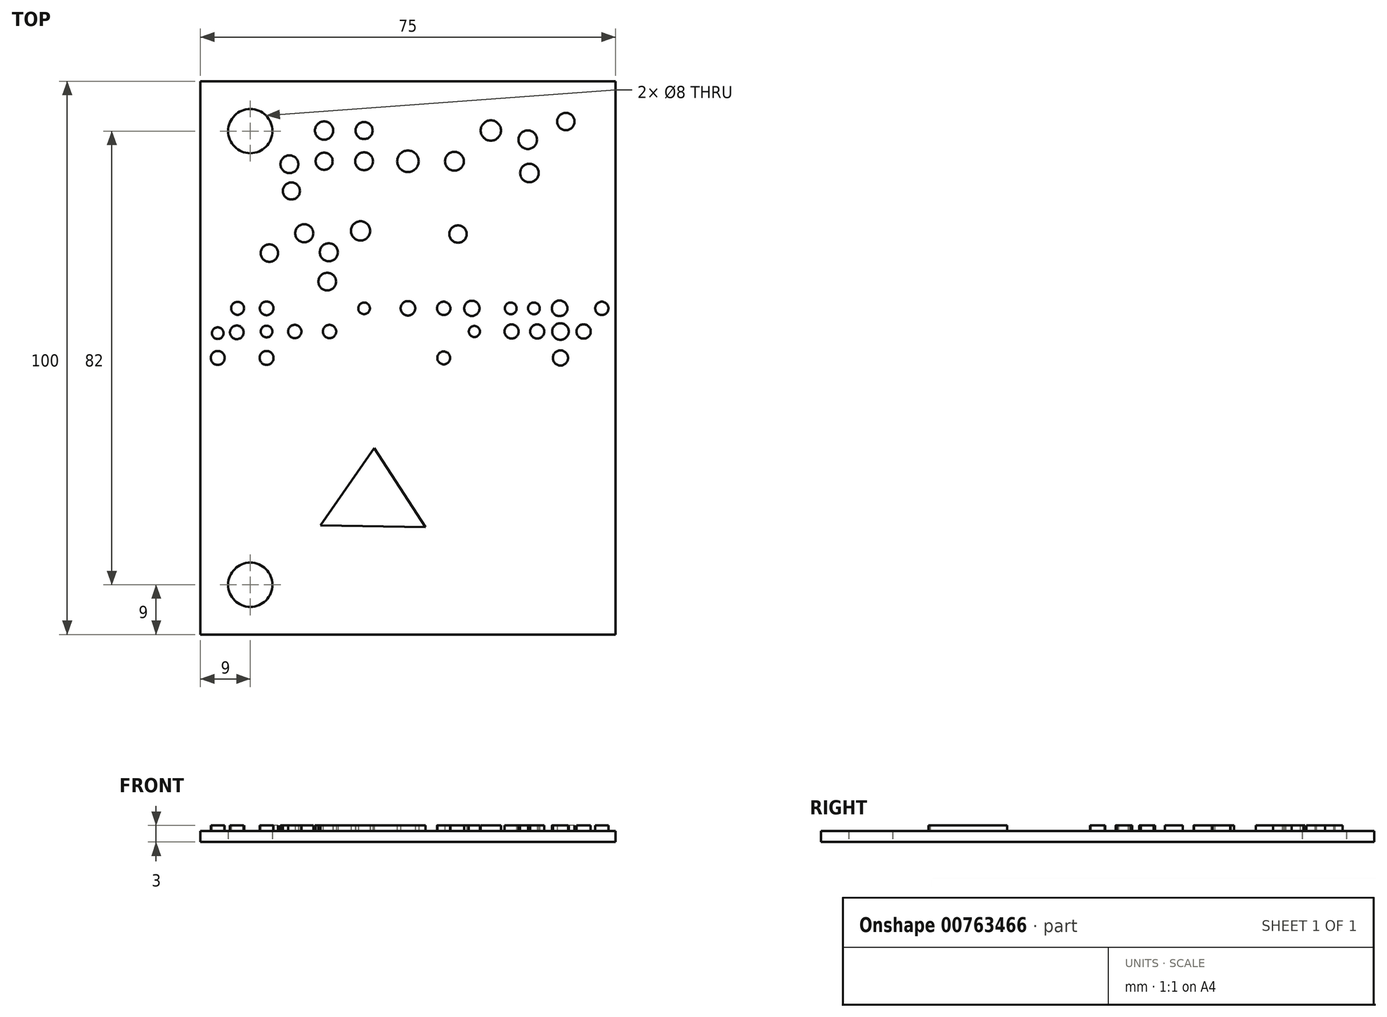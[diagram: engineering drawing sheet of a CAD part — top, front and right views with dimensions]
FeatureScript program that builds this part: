
annotation { "Feature Type Name" : "Feature", "Feature Type Description" : "" }
export const myFeature = defineFeature(function(context is Context, id is Id, definition is map)
    precondition{}
    {
        {
            var Q0;
            Q0=qCreatedBy(makeId("Top.planeOp"),FACE);
            var sketch = newSketch(context, id + "F0", { "sketchPlane" : qUnion([Q0])});
            skLineSegment(sketch, "E0.bottom", {"start": v(-37.5, 50) * mm, "end": v(37.5, 50) * mm});
            skLineSegment(sketch, "E0.top", {"start": v(-37.5, -50) * mm, "end": v(37.5, -50) * mm});
            skLineSegment(sketch, "E0.left", {"start": v(-37.5, 50) * mm, "end": v(-37.5, -50) * mm});
            skLineSegment(sketch, "E0.right", {"start": v(37.5, 50) * mm, "end": v(37.5, -50) * mm});
            skPoint(sketch, "E0.middle", {"position": v(0, 0) * mm});
            skCircle(sketch, "E1", {"center": v(-28.5, -41) * mm, "radius": 4 * mm});
            skCircle(sketch, "E2", {"center": v(-28.5, 41) * mm, "radius": 4 * mm});
            skSolve(sketch);
        }
        {
            var Q0;
            Q0=makeQuery(id+"F0.imprint","IMPRINT",FACE,{"disambiguationData":[TD([[makeQuery(id+"F0.imprint","IMPRINT",EDGE,{"derivedFrom":sQuery(id+"F0.wireOp",EDGE,"E0.bottom")}),-1.0]])]});
            extrude(context, id + "F1", {"entities" : qUnion([Q0]), "depth" : 2 * mm, "offsetDistance" : 25 * mm});
        }
        {
            var Q0;
            Q0=makeQuery(id+"F1.opExtrude","CAP_FACE",FACE,{"disambiguationData":[OSD([sQuery(id+"F0.wireOp",EDGE,"E0.bottom"),sQuery(id+"F0.wireOp",EDGE,"E0.top"),sQuery(id+"F0.wireOp",EDGE,"E0.left"),sQuery(id+"F0.wireOp",EDGE,"E0.right"),sQuery(id+"F0.wireOp",EDGE,"E1"),sQuery(id+"F0.wireOp",EDGE,"E2")])],"isStart":false});
            var sketch = newSketch(context, id + "F2", { "sketchPlane" : qUnion([Q0])});
            skCircle(sketch, "E3", {"center": v(-21.07, 30.18) * mm, "radius": 1.54 * mm});
            skCircle(sketch, "E4", {"center": v(-21.43, 35.01) * mm, "radius": 1.61 * mm});
            skCircle(sketch, "E5", {"center": v(-15.15, 35.55) * mm, "radius": 1.54 * mm});
            skCircle(sketch, "E6", {"center": v(-15.15, 41.1) * mm, "radius": 1.65 * mm});
            skCircle(sketch, "E7", {"center": v(-7.93, 35.55) * mm, "radius": 1.61 * mm});
            skCircle(sketch, "E8", {"center": v(0, 35.55) * mm, "radius": 1.94 * mm});
            skCircle(sketch, "E9", {"center": v(-7.93, 41.1) * mm, "radius": 1.55 * mm});
            skCircle(sketch, "E10", {"center": v(8.4, 35.55) * mm, "radius": 1.7 * mm});
            skCircle(sketch, "E11", {"center": v(14.99, 41.1) * mm, "radius": 1.83 * mm});
            skCircle(sketch, "E12", {"center": v(21.95, 33.42) * mm, "radius": 1.67 * mm});
            skCircle(sketch, "E13", {"center": v(21.67, 39.44) * mm, "radius": 1.68 * mm});
            skCircle(sketch, "E14", {"center": v(28.55, 42.74) * mm, "radius": 1.58 * mm});
            skCircle(sketch, "E15", {"center": v(-25.05, 18.95) * mm, "radius": 1.58 * mm});
            skCircle(sketch, "E16", {"center": v(-18.74, 22.53) * mm, "radius": 1.63 * mm});
            skCircle(sketch, "E17", {"center": v(-14.59, 13.8) * mm, "radius": 1.6 * mm});
            skCircle(sketch, "E18", {"center": v(-14.3, 19.1) * mm, "radius": 1.63 * mm});
            skCircle(sketch, "E19", {"center": v(-8.57, 22.96) * mm, "radius": 1.75 * mm});
            skCircle(sketch, "E20", {"center": v(9.06, 22.39) * mm, "radius": 1.58 * mm});
            skCircle(sketch, "E21", {"center": v(-34.38, 0) * mm, "radius": 1.26 * mm});
            skCircle(sketch, "E22", {"center": v(-34.38, 4.48) * mm, "radius": 1.06 * mm});
            skCircle(sketch, "E23", {"center": v(-30.94, 4.63) * mm, "radius": 1.23 * mm});
            skCircle(sketch, "E24", {"center": v(-30.8, 8.97) * mm, "radius": 1.17 * mm});
            skCircle(sketch, "E25", {"center": v(-25.55, 0) * mm, "radius": 1.26 * mm});
            skCircle(sketch, "E26", {"center": v(-25.55, 4.78) * mm, "radius": 1.06 * mm});
            skCircle(sketch, "E27", {"center": v(-25.55, 8.97) * mm, "radius": 1.23 * mm});
            skCircle(sketch, "E28", {"center": v(-20.47, 4.78) * mm, "radius": 1.2 * mm});
            skCircle(sketch, "E29", {"center": v(-14.18, 4.78) * mm, "radius": 1.2 * mm});
            skCircle(sketch, "E30", {"center": v(-7.93, 8.97) * mm, "radius": 1.05 * mm});
            skCircle(sketch, "E31", {"center": v(0, 8.97) * mm, "radius": 1.31 * mm});
            skCircle(sketch, "E32", {"center": v(6.47, 0) * mm, "radius": 1.16 * mm});
            skCircle(sketch, "E33", {"center": v(6.47, 8.97) * mm, "radius": 1.2 * mm});
            skCircle(sketch, "E34", {"center": v(11.56, 8.97) * mm, "radius": 1.38 * mm});
            skCircle(sketch, "E35", {"center": v(12, 4.78) * mm, "radius": 1 * mm});
            skCircle(sketch, "E36", {"center": v(18.74, 4.78) * mm, "radius": 1.28 * mm});
            skCircle(sketch, "E37", {"center": v(18.6, 8.97) * mm, "radius": 1.06 * mm});
            skCircle(sketch, "E38", {"center": v(22.78, 8.97) * mm, "radius": 1.06 * mm});
            skCircle(sketch, "E39", {"center": v(23.38, 4.78) * mm, "radius": 1.28 * mm});
            skCircle(sketch, "E40", {"center": v(27.42, 8.97) * mm, "radius": 1.41 * mm});
            skCircle(sketch, "E41", {"center": v(27.57, 4.78) * mm, "radius": 1.5 * mm});
            skCircle(sketch, "E42", {"center": v(27.57, 0) * mm, "radius": 1.37 * mm});
            skCircle(sketch, "E43", {"center": v(31.76, 4.78) * mm, "radius": 1.29 * mm});
            skCircle(sketch, "E44", {"center": v(35.05, 8.97) * mm, "radius": 1.2 * mm});
            skLineSegment(sketch, "E45", {"start": v(-15.8, -30.26) * mm, "end": v(-6.08, -16.31) * mm});
            skLineSegment(sketch, "E46", {"start": v(-6.08, -16.31) * mm, "end": v(3.2, -30.56) * mm});
            skLineSegment(sketch, "E47", {"start": v(3.2, -30.56) * mm, "end": v(-15.8, -30.26) * mm});
            skSolve(sketch);
        }
        {
            var Q0;
            Q0=makeQuery(id+"F2.imprint","IMPRINT",FACE,{"disambiguationData":[TD([[makeQuery(id+"F2.imprint","IMPRINT",EDGE,{"derivedFrom":sQuery(id+"F2.wireOp",EDGE,"E45")}),-1.0]])]});
            var Q1;
            Q1=makeQuery(id+"F2.imprint","IMPRINT",FACE,{"disambiguationData":[TD([[makeQuery(id+"F2.imprint","IMPRINT",EDGE,{"derivedFrom":sQuery(id+"F2.wireOp",EDGE,"E21")}),1.0]])]});
            var Q2;
            Q2=makeQuery(id+"F2.imprint","IMPRINT",FACE,{"disambiguationData":[TD([[makeQuery(id+"F2.imprint","IMPRINT",EDGE,{"derivedFrom":sQuery(id+"F2.wireOp",EDGE,"E22")}),1.0]])]});
            var Q3;
            Q3=makeQuery(id+"F2.imprint","IMPRINT",FACE,{"disambiguationData":[TD([[makeQuery(id+"F2.imprint","IMPRINT",EDGE,{"derivedFrom":sQuery(id+"F2.wireOp",EDGE,"E23")}),1.0]])]});
            var Q4;
            Q4=makeQuery(id+"F2.imprint","IMPRINT",FACE,{"disambiguationData":[TD([[makeQuery(id+"F2.imprint","IMPRINT",EDGE,{"derivedFrom":sQuery(id+"F2.wireOp",EDGE,"E25")}),1.0]])]});
            var Q5;
            Q5=makeQuery(id+"F2.imprint","IMPRINT",FACE,{"disambiguationData":[TD([[makeQuery(id+"F2.imprint","IMPRINT",EDGE,{"derivedFrom":sQuery(id+"F2.wireOp",EDGE,"E24")}),1.0]])]});
            var Q6;
            Q6=makeQuery(id+"F2.imprint","IMPRINT",FACE,{"disambiguationData":[TD([[makeQuery(id+"F2.imprint","IMPRINT",EDGE,{"derivedFrom":sQuery(id+"F2.wireOp",EDGE,"E27")}),1.0]])]});
            var Q7;
            Q7=makeQuery(id+"F2.imprint","IMPRINT",FACE,{"disambiguationData":[TD([[makeQuery(id+"F2.imprint","IMPRINT",EDGE,{"derivedFrom":sQuery(id+"F2.wireOp",EDGE,"E26")}),1.0]])]});
            var Q8;
            Q8=makeQuery(id+"F2.imprint","IMPRINT",FACE,{"disambiguationData":[TD([[makeQuery(id+"F2.imprint","IMPRINT",EDGE,{"derivedFrom":sQuery(id+"F2.wireOp",EDGE,"E28")}),1.0]])]});
            var Q9;
            Q9=makeQuery(id+"F2.imprint","IMPRINT",FACE,{"disambiguationData":[TD([[makeQuery(id+"F2.imprint","IMPRINT",EDGE,{"derivedFrom":sQuery(id+"F2.wireOp",EDGE,"E29")}),1.0]])]});
            var Q10;
            Q10=makeQuery(id+"F2.imprint","IMPRINT",FACE,{"disambiguationData":[TD([[makeQuery(id+"F2.imprint","IMPRINT",EDGE,{"derivedFrom":sQuery(id+"F2.wireOp",EDGE,"E30")}),1.0]])]});
            var Q11;
            Q11=makeQuery(id+"F2.imprint","IMPRINT",FACE,{"disambiguationData":[TD([[makeQuery(id+"F2.imprint","IMPRINT",EDGE,{"derivedFrom":sQuery(id+"F2.wireOp",EDGE,"E17")}),1.0]])]});
            var Q12;
            Q12=makeQuery(id+"F2.imprint","IMPRINT",FACE,{"disambiguationData":[TD([[makeQuery(id+"F2.imprint","IMPRINT",EDGE,{"derivedFrom":sQuery(id+"F2.wireOp",EDGE,"E15")}),1.0]])]});
            var Q13;
            Q13=makeQuery(id+"F2.imprint","IMPRINT",FACE,{"disambiguationData":[TD([[makeQuery(id+"F2.imprint","IMPRINT",EDGE,{"derivedFrom":sQuery(id+"F2.wireOp",EDGE,"E16")}),1.0]])]});
            var Q14;
            Q14=makeQuery(id+"F2.imprint","IMPRINT",FACE,{"disambiguationData":[TD([[makeQuery(id+"F2.imprint","IMPRINT",EDGE,{"derivedFrom":sQuery(id+"F2.wireOp",EDGE,"E19")}),1.0]])]});
            var Q15;
            Q15=makeQuery(id+"F2.imprint","IMPRINT",FACE,{"disambiguationData":[TD([[makeQuery(id+"F2.imprint","IMPRINT",EDGE,{"derivedFrom":sQuery(id+"F2.wireOp",EDGE,"E18")}),1.0]])]});
            var Q16;
            Q16=makeQuery(id+"F2.imprint","IMPRINT",FACE,{"disambiguationData":[TD([[makeQuery(id+"F2.imprint","IMPRINT",EDGE,{"derivedFrom":sQuery(id+"F2.wireOp",EDGE,"E31")}),1.0]])]});
            var Q17;
            Q17=makeQuery(id+"F2.imprint","IMPRINT",FACE,{"disambiguationData":[TD([[makeQuery(id+"F2.imprint","IMPRINT",EDGE,{"derivedFrom":sQuery(id+"F2.wireOp",EDGE,"E33")}),1.0]])]});
            var Q18;
            Q18=makeQuery(id+"F2.imprint","IMPRINT",FACE,{"disambiguationData":[TD([[makeQuery(id+"F2.imprint","IMPRINT",EDGE,{"derivedFrom":sQuery(id+"F2.wireOp",EDGE,"E34")}),1.0]])]});
            var Q19;
            Q19=makeQuery(id+"F2.imprint","IMPRINT",FACE,{"disambiguationData":[TD([[makeQuery(id+"F2.imprint","IMPRINT",EDGE,{"derivedFrom":sQuery(id+"F2.wireOp",EDGE,"E32")}),1.0]])]});
            var Q20;
            Q20=makeQuery(id+"F2.imprint","IMPRINT",FACE,{"disambiguationData":[TD([[makeQuery(id+"F2.imprint","IMPRINT",EDGE,{"derivedFrom":sQuery(id+"F2.wireOp",EDGE,"E35")}),1.0]])]});
            var Q21;
            Q21=makeQuery(id+"F2.imprint","IMPRINT",FACE,{"disambiguationData":[TD([[makeQuery(id+"F2.imprint","IMPRINT",EDGE,{"derivedFrom":sQuery(id+"F2.wireOp",EDGE,"E37")}),1.0]])]});
            var Q22;
            Q22=makeQuery(id+"F2.imprint","IMPRINT",FACE,{"disambiguationData":[TD([[makeQuery(id+"F2.imprint","IMPRINT",EDGE,{"derivedFrom":sQuery(id+"F2.wireOp",EDGE,"E38")}),1.0]])]});
            var Q23;
            Q23=makeQuery(id+"F2.imprint","IMPRINT",FACE,{"disambiguationData":[TD([[makeQuery(id+"F2.imprint","IMPRINT",EDGE,{"derivedFrom":sQuery(id+"F2.wireOp",EDGE,"E40")}),1.0]])]});
            var Q24;
            Q24=makeQuery(id+"F2.imprint","IMPRINT",FACE,{"disambiguationData":[TD([[makeQuery(id+"F2.imprint","IMPRINT",EDGE,{"derivedFrom":sQuery(id+"F2.wireOp",EDGE,"E44")}),1.0]])]});
            var Q25;
            Q25=makeQuery(id+"F2.imprint","IMPRINT",FACE,{"disambiguationData":[TD([[makeQuery(id+"F2.imprint","IMPRINT",EDGE,{"derivedFrom":sQuery(id+"F2.wireOp",EDGE,"E43")}),1.0]])]});
            var Q26;
            Q26=makeQuery(id+"F2.imprint","IMPRINT",FACE,{"disambiguationData":[TD([[makeQuery(id+"F2.imprint","IMPRINT",EDGE,{"derivedFrom":sQuery(id+"F2.wireOp",EDGE,"E41")}),1.0]])]});
            var Q27;
            Q27=makeQuery(id+"F2.imprint","IMPRINT",FACE,{"disambiguationData":[TD([[makeQuery(id+"F2.imprint","IMPRINT",EDGE,{"derivedFrom":sQuery(id+"F2.wireOp",EDGE,"E36")}),1.0]])]});
            var Q28;
            Q28=makeQuery(id+"F2.imprint","IMPRINT",FACE,{"disambiguationData":[TD([[makeQuery(id+"F2.imprint","IMPRINT",EDGE,{"derivedFrom":sQuery(id+"F2.wireOp",EDGE,"E39")}),1.0]])]});
            var Q29;
            Q29=makeQuery(id+"F2.imprint","IMPRINT",FACE,{"disambiguationData":[TD([[makeQuery(id+"F2.imprint","IMPRINT",EDGE,{"derivedFrom":sQuery(id+"F2.wireOp",EDGE,"E42")}),1.0]])]});
            var Q30;
            Q30=makeQuery(id+"F2.imprint","IMPRINT",FACE,{"disambiguationData":[TD([[makeQuery(id+"F2.imprint","IMPRINT",EDGE,{"derivedFrom":sQuery(id+"F2.wireOp",EDGE,"E20")}),1.0]])]});
            var Q31;
            Q31=makeQuery(id+"F2.imprint","IMPRINT",FACE,{"disambiguationData":[TD([[makeQuery(id+"F2.imprint","IMPRINT",EDGE,{"derivedFrom":sQuery(id+"F2.wireOp",EDGE,"E10")}),1.0]])]});
            var Q32;
            Q32=makeQuery(id+"F2.imprint","IMPRINT",FACE,{"disambiguationData":[TD([[makeQuery(id+"F2.imprint","IMPRINT",EDGE,{"derivedFrom":sQuery(id+"F2.wireOp",EDGE,"E8")}),1.0]])]});
            var Q33;
            Q33=makeQuery(id+"F2.imprint","IMPRINT",FACE,{"disambiguationData":[TD([[makeQuery(id+"F2.imprint","IMPRINT",EDGE,{"derivedFrom":sQuery(id+"F2.wireOp",EDGE,"E7")}),1.0]])]});
            var Q34;
            Q34=makeQuery(id+"F2.imprint","IMPRINT",FACE,{"disambiguationData":[TD([[makeQuery(id+"F2.imprint","IMPRINT",EDGE,{"derivedFrom":sQuery(id+"F2.wireOp",EDGE,"E5")}),1.0]])]});
            var Q35;
            Q35=makeQuery(id+"F2.imprint","IMPRINT",FACE,{"disambiguationData":[TD([[makeQuery(id+"F2.imprint","IMPRINT",EDGE,{"derivedFrom":sQuery(id+"F2.wireOp",EDGE,"E6")}),1.0]])]});
            var Q36;
            Q36=makeQuery(id+"F2.imprint","IMPRINT",FACE,{"disambiguationData":[TD([[makeQuery(id+"F2.imprint","IMPRINT",EDGE,{"derivedFrom":sQuery(id+"F2.wireOp",EDGE,"E9")}),1.0]])]});
            var Q37;
            Q37=makeQuery(id+"F2.imprint","IMPRINT",FACE,{"disambiguationData":[TD([[makeQuery(id+"F2.imprint","IMPRINT",EDGE,{"derivedFrom":sQuery(id+"F2.wireOp",EDGE,"E11")}),1.0]])]});
            var Q38;
            Q38=makeQuery(id+"F2.imprint","IMPRINT",FACE,{"disambiguationData":[TD([[makeQuery(id+"F2.imprint","IMPRINT",EDGE,{"derivedFrom":sQuery(id+"F2.wireOp",EDGE,"E13")}),1.0]])]});
            var Q39;
            Q39=makeQuery(id+"F2.imprint","IMPRINT",FACE,{"disambiguationData":[TD([[makeQuery(id+"F2.imprint","IMPRINT",EDGE,{"derivedFrom":sQuery(id+"F2.wireOp",EDGE,"E12")}),1.0]])]});
            var Q40;
            Q40=makeQuery(id+"F2.imprint","IMPRINT",FACE,{"disambiguationData":[TD([[makeQuery(id+"F2.imprint","IMPRINT",EDGE,{"derivedFrom":sQuery(id+"F2.wireOp",EDGE,"E14")}),1.0]])]});
            var Q41;
            Q41=makeQuery(id+"F2.imprint","IMPRINT",FACE,{"disambiguationData":[TD([[makeQuery(id+"F2.imprint","IMPRINT",EDGE,{"derivedFrom":sQuery(id+"F2.wireOp",EDGE,"E3")}),1.0]])]});
            var Q42;
            Q42=makeQuery(id+"F2.imprint","IMPRINT",FACE,{"disambiguationData":[TD([[makeQuery(id+"F2.imprint","IMPRINT",EDGE,{"derivedFrom":sQuery(id+"F2.wireOp",EDGE,"E4")}),1.0]])]});
            extrude(context, id + "F3", {"entities" : qUnion([Q0, Q1, Q2, Q3, Q4, Q5, Q6, Q7, Q8, Q9, Q10, Q11, Q12, Q13, Q14, Q15, Q16, Q17, Q18, Q19, Q20, Q21, Q22, Q23, Q24, Q25, Q26, Q27, Q28, Q29, Q30, Q31, Q32, Q33, Q34, Q35, Q36, Q37, Q38, Q39, Q40, Q41, Q42]), "operationType" : NewBodyOperationType.ADD, "depth" : 1 * mm, "offsetDistance" : 25 * mm});
        }
    });
